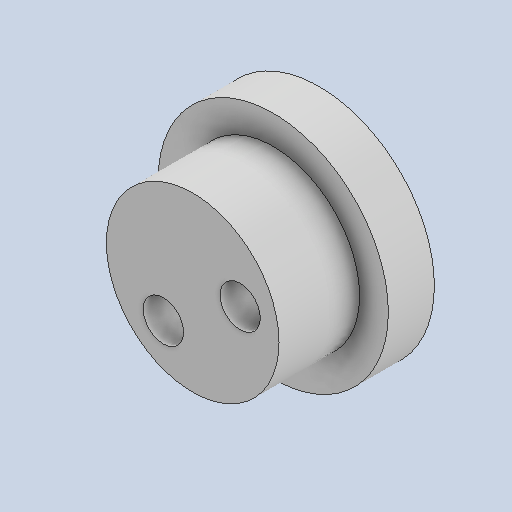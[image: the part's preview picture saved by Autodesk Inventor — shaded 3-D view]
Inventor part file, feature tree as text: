
AUTODESK INVENTOR PART (.ipt)
format: ipt  version: 2023 (Build 270158000, 158)  size: 159,744 bytes
history: native  units: in
note: dims shown in document units (in); Inventor stores cm internally (conversion verified against a paired STEP export)
features: reference x3, other x3, extrude x2, sketch x2, projected_geometry x1
ambient origin geometry x8: Origin, YZ Plane, XZ Plane, XY Plane, X Axis, Y Axis, Z Axis, Center Point
bodies: Solid1 (feature_tree)
feature tree (11):
  extrude  "Extrusion1"  Depth=0.0591in
  extrude  "Extrusion2"  Depth=0.2756in
  sketch  "Sketch3"  dims[d1=0.0591in d2=0.7874in]
  reference  "Reference1"
  reference  "Reference2"
  reference  "Reference3"
  sketch  "Sketch4"  dims[d4=0.1575in d5=0.0in d6=0.5906in d7=0.2756in d8=0.0in d9=0.315in]
  projected_geometry  "Projected Loop1"
  other  "<userpath>\OneDrive\Documents\Robotics Club\Cycloidal Drive\Drive.iam"
  other  "Drive.iam"
  other  "Shaft-1:1"
